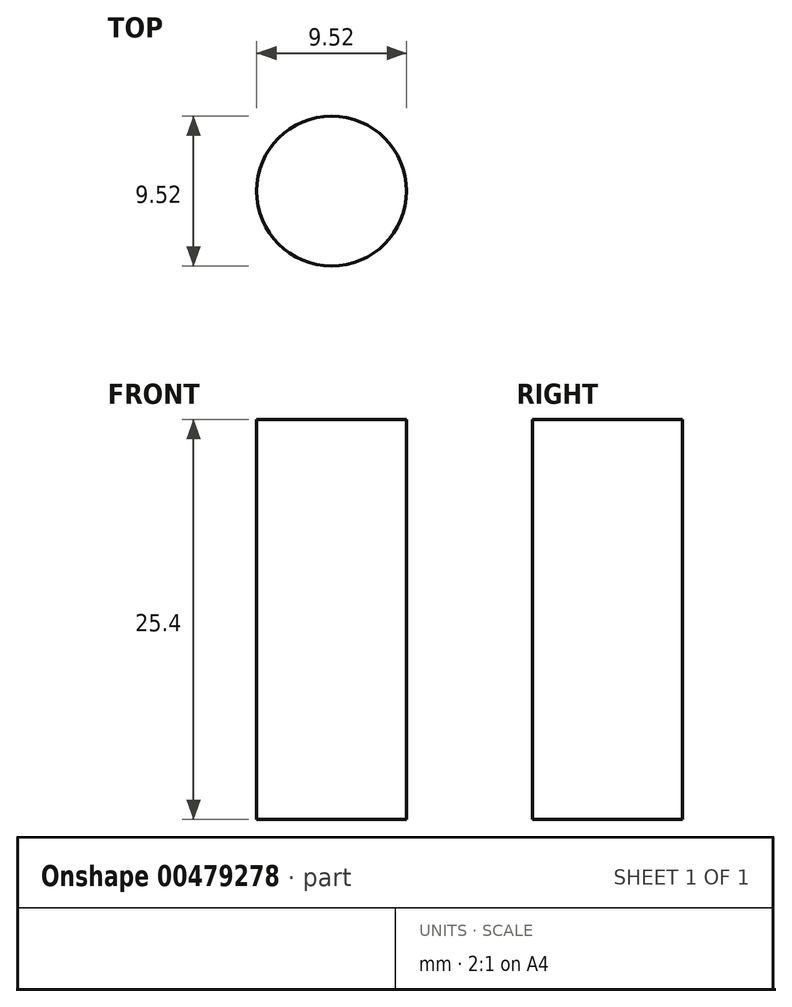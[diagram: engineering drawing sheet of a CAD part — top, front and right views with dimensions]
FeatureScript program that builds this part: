
annotation { "Feature Type Name" : "Feature", "Feature Type Description" : "" }
export const myFeature = defineFeature(function(context is Context, id is Id, definition is map)
    precondition{}
    {
        {
            var Q0;
            Q0=qCreatedBy(makeId("Top.planeOp"),FACE);
            var sketch = newSketch(context, id + "F0", { "sketchPlane" : qUnion([Q0])});
            skCircle(sketch, "E0", {"center": v(-15.37, 7.91) * mm, "radius": 4.76 * mm});
            skSolve(sketch);
        }
        {
            var Q0;
            Q0=makeQuery(id+"F0.imprint","IMPRINT",FACE,{"disambiguationData":[TD([[makeQuery(id+"F0.imprint","IMPRINT",EDGE,{"derivedFrom":sQuery(id+"F0.wireOp",EDGE,"E0")}),1.0]])]});
            extrude(context, id + "F1", {"entities" : qUnion([Q0]), "depth" : 25.4 * mm});
        }
    });
